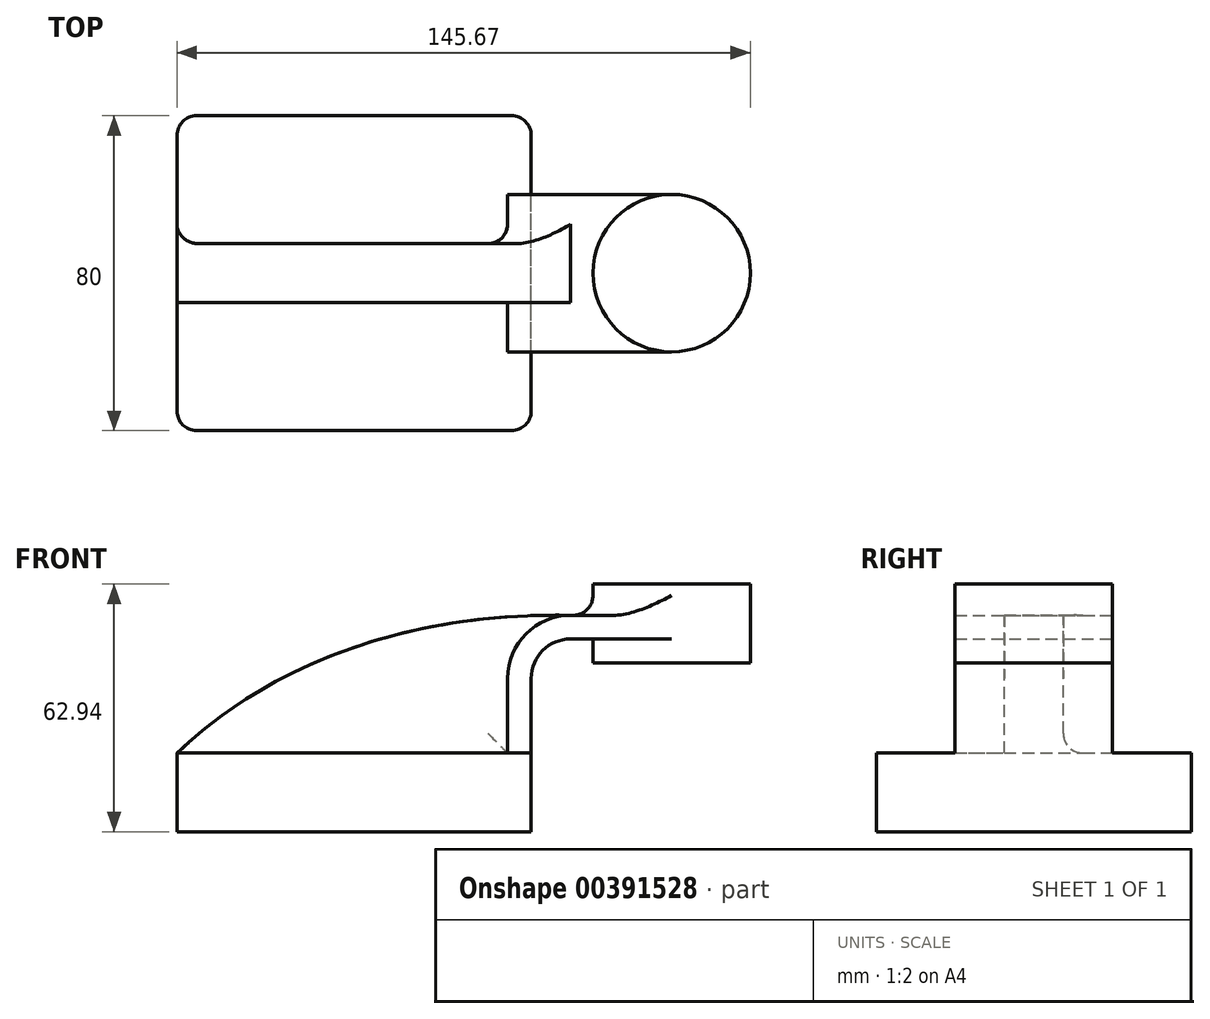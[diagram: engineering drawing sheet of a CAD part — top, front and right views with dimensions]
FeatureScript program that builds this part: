
annotation { "Feature Type Name" : "Feature", "Feature Type Description" : "" }
export const myFeature = defineFeature(function(context is Context, id is Id, definition is map)
    precondition{}
    {
        {
            var Q0;
            Q0=qCreatedBy(makeId("Front.planeOp"),FACE);
            var sketch = newSketch(context, id + "F0", { "sketchPlane" : qUnion([Q0])});
            skLineSegment(sketch, "E0.bottom", {"start": v(-45, 10) * mm, "end": v(45, 10) * mm});
            skLineSegment(sketch, "E0.top", {"start": v(-45, -10) * mm, "end": v(45, -10) * mm});
            skLineSegment(sketch, "E0.left", {"start": v(-45, 10) * mm, "end": v(-45, -10) * mm});
            skLineSegment(sketch, "E0.right", {"start": v(45, 10) * mm, "end": v(45, -10) * mm});
            skPoint(sketch, "E0.middle", {"position": v(0, 0) * mm});
            skLineSegment(sketch, "E1.bottom", {"start": v(60.67, 32.94) * mm, "end": v(100.67, 32.94) * mm});
            skLineSegment(sketch, "E1.top", {"start": v(60.67, 52.94) * mm, "end": v(100.67, 52.94) * mm});
            skLineSegment(sketch, "E1.left", {"start": v(60.67, 32.94) * mm, "end": v(60.67, 52.94) * mm});
            skLineSegment(sketch, "E1.right", {"start": v(100.67, 32.94) * mm, "end": v(100.67, 52.94) * mm});
            skPoint(sketch, "E1.middle", {"position": v(80.67, 42.94) * mm});
            skLineSegment(sketch, "E2", {"start": v(45, 10) * mm, "end": v(45, 29) * mm});
            skArc(sketch, "E3", {"start": v(45, 29) * mm, "mid": v(47.93, 36.07) * mm, "end": v(55, 39) * mm});
            skLineSegment(sketch, "E4", {"start": v(80.67, 39) * mm, "end": v(55, 39) * mm});
            skLineSegment(sketch, "E5.0", {"start": v(39, 10) * mm, "end": v(39, 29) * mm});
            skArc(sketch, "E5.1", {"start": v(39, 29) * mm, "mid": v(43.69, 40.31) * mm, "end": v(55, 45) * mm});
            skLineSegment(sketch, "E5.2", {"start": v(80.67, 45) * mm, "end": v(55, 45) * mm});
            skFitSpline(sketch, "E6", {"points": [v(-45, 10) * mm, v(55, 45) * mm], "startDerivative": vector(12.16, 10.29) * mm, "endDerivative": vector(194.56, -3.77) * mm});
            skLineSegment(sketch, "E7", {"start": v(80.67, 52.94) * mm, "end": v(80.67, 32.94) * mm});
            skSolve(sketch);
        }
        {
            var Q0;
            Q0=makeQuery(id+"F0.imprint","IMPRINT",FACE,{"disambiguationData":[TD([[makeQuery(id+"F0.imprint","IMPRINT",EDGE,{"derivedFrom":sQuery(id+"F0.wireOp",EDGE,"E0.top")}),1.0]])]});
            extrude(context, id + "F1", {"entities" : qUnion([Q0]), "endBound" : BoundingType.SYMMETRIC, "depth" : 80 * mm});
        }
        {
            var Q0;
            {var subQ1=sQuery(id+"F0.wireOp",EDGE,"E2");Q0=makeQuery(id+"F0.imprint","IMPRINT",FACE,{"disambiguationData":[TD([[makeQuery(id+"F0.imprint","IMPRINT",EDGE,{"derivedFrom":subQ1}),1.0]])]});}
            var Q1;
            {var subQ0=sQuery(id+"F0.wireOp",EDGE,"E4");var subQ1=sQuery(id+"F0.wireOp",EDGE,"E1.left");var subQ2=makeQuery(id+"F0.imprint","INTERSECT",VERTEX,{"derivedFrom":[subQ1,subQ0]});Q1=makeQuery(id+"F0.imprint","IMPRINT",FACE,{"disambiguationData":[TD([[makeQuery(id+"F0.imprint","IMPRINT",EDGE,{"disambiguationData":[TD([[subQ2,-1.0]])],"derivedFrom":subQ1}),-1.0]])]});}
            extrude(context, id + "F2", {"entities" : qUnion([Q0, Q1]), "operationType" : NewBodyOperationType.ADD, "endBound" : BoundingType.SYMMETRIC, "depth" : 40 * mm});
        }
        {
            var Q0;
            {var subQ2=sQuery(id+"F0.wireOp",EDGE,"E5.0");Q0=makeQuery(id+"F0.imprint","IMPRINT",FACE,{"disambiguationData":[TD([[makeQuery(id+"F0.imprint","IMPRINT",EDGE,{"derivedFrom":subQ2}),1.0]])]});}
            extrude(context, id + "F3", {"entities" : qUnion([Q0]), "operationType" : NewBodyOperationType.ADD, "endBound" : BoundingType.SYMMETRIC, "depth" : 15 * mm});
        }
        {
            var Q0;
            {var subQ4=sQuery(id+"F0.wireOp",EDGE,"E1.right");Q0=makeQuery(id+"F0.imprint","IMPRINT",FACE,{"disambiguationData":[TD([[makeQuery(id+"F0.imprint","IMPRINT",EDGE,{"derivedFrom":subQ4}),1.0]])]});}
            var Q1;
            Q1=sQuery(id+"F0.wireOp",EDGE,"E7");
            revolve(context, id + "F4", {"operationType" : NewBodyOperationType.ADD, "entities" : qUnion([Q0]), "axis" : qUnion([Q1]), "revolveType" : RevolveType.FULL});
        }
        {
            var Q0;
            Q0=makeQuery(id+"F1.opExtrude","CAP_EDGE",EDGE,{"disambiguationData":[OSD([sQuery(id+"F0.wireOp",EDGE,"E0.right")])],"isStart":false});
            var Q1;
            Q1=makeQuery(id+"F1.opExtrude","CAP_EDGE",EDGE,{"disambiguationData":[OSD([sQuery(id+"F0.wireOp",EDGE,"E0.left")])],"isStart":false});
            var Q2;
            Q2=makeQuery(id+"F1.opExtrude","CAP_EDGE",EDGE,{"disambiguationData":[OSD([sQuery(id+"F0.wireOp",EDGE,"E0.left")])],"isStart":true});
            var Q3;
            Q3=makeQuery(id+"F1.opExtrude","CAP_EDGE",EDGE,{"disambiguationData":[OSD([sQuery(id+"F0.wireOp",EDGE,"E0.right")])],"isStart":true});
            fillet(context, id + "F5", {"entities" : qUnion([Q0, Q1, Q2, Q3]), "radius" : 5 * mm, "tangentPropagation" : true, "allowEdgeOverflow" : false});
        }
        {
            var Q0;
            Q0=makeQuery(id+"F3.opExtrude","CAP_EDGE",EDGE,{"disambiguationData":[OSD([sQuery(id+"F0.wireOp",EDGE,"E0.bottom")])],"isStart":true});
            var Q1;
            Q1=makeQuery(id+"F3.opExtrude","CAP_EDGE",EDGE,{"disambiguationData":[OSD([sQuery(id+"F0.wireOp",EDGE,"E5.0")])],"isStart":true});
            var Q2;
            Q2=makeQuery(id+"F3.opExtrude","CAP_EDGE",EDGE,{"disambiguationData":[OSD([sQuery(id+"F0.wireOp",EDGE,"E5.1")])],"isStart":true});
            var Q3;
            Q3=makeQuery(id+"F3.opExtrude","CAP_EDGE",EDGE,{"disambiguationData":[OSD([sQuery(id+"F0.wireOp",EDGE,"E0.bottom")])],"isStart":false});
            var Q4;
            Q4=makeQuery(id+"F3.opExtrude","CAP_EDGE",EDGE,{"disambiguationData":[OSD([sQuery(id+"F0.wireOp",EDGE,"E5.0")])],"isStart":false});
            var Q5;
            Q5=makeQuery(id+"F3.opExtrude","CAP_EDGE",EDGE,{"disambiguationData":[OSD([sQuery(id+"F0.wireOp",EDGE,"E5.1")])],"isStart":false});
            var Q6;
            Q6=makeQuery(id+"F4.boolean.opBoolean","INTERSECT",EDGE,{"derivedFrom":[makeQuery(id+"F2.opExtrude","SWEPT_FACE",FACE,{"disambiguationData":[OSD([sQuery(id+"F0.wireOp",EDGE,"E5.2")])]}),makeQuery(id+"F4.opRevolve","SWEPT_FACE",FACE,{"disambiguationData":[OSD([sQuery(id+"F0.wireOp",EDGE,"E1.right")])]})]});
            fillet(context, id + "F6", {"entities" : qUnion([Q0, Q1, Q2, Q3, Q4, Q5, Q6]), "radius" : 5 * mm, "tangentPropagation" : true, "allowEdgeOverflow" : false});
        }
    });
